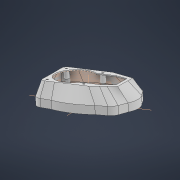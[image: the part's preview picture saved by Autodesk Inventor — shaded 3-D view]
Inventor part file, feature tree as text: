
AUTODESK INVENTOR PART (.ipt)
format: ipt  version: 2021 (Build 250183000, 183)  size: 3,913,216 bytes
history: native  units: mm
features: sketch x6, other x5, extrude x3, plane x2, surface_op x2, thicken_offset x1, loft x1
ambient origin geometry x8: Origin, YZ Plane, XZ Plane, XY Plane, X Axis, Y Axis, Z Axis, Center Point
bodies: Solid1 (feature_tree)
feature tree (20):
  sketch  "Sketch7"  dims[d14=167.0mm d15=119.0mm d16=3.8mm d18=3.8mm d19=3.8mm d20=3.8mm d22=5.0mm d23=10.0mm d24=10.0mm d25=10.0mm d26=10.0mm d27=12.0mm d28=12.0mm d29=12.0mm d30=12.0mm d31=-34.0mm d32=27.925268mm d33=118.0mm d34=82.0mm d35=10.0mm d47=10.0mm d48=10.0mm d49=100.0mm d50=25.0mm d51=25.0mm d52=8.0mm d53=8.0mm d54=0.0mm d55=90.0deg d56=0.0mm d57=90.0deg d58=10.0mm d59=0.0mm d60=2.49mm d61=20.0mm d62=20.0mm d63=0.0mm d64=20.0mm d65=0.0mm]
  plane  "Work Plane1"
  sketch  "Sketch2"  dims[d2=5.8mm d4=45.0deg]
  sketch  "Sketch1"  dims[d0=54.0mm d1=127.0mm]
  plane  "Work Plane2"
  sketch  "Sketch4"  dims[d11=83.5mm d12=59.5mm]
  sketch  "Sketch3"  dims[d6=40.0mm d8=360.0deg d10=83.5mm]
  surface_op  "Stitch Surface1"
  thicken_offset  "Thicken1"
  extrude  "Extrusion1"  Depth=127.0mm
  extrude  "Extrusion2"  TaperAngle=45.0deg  [1 undecoded]
  other  "Srf4"
  other  "Srf5"
  other  "Srf6"
  other  "Srf7"
  sketch  "Sketch6"  dims[d13=59.5mm]
  other  "Image1"
  loft  "LoftSrf2"
  extrude  "ExtrusionSrf2"  Depth=59.5mm
  surface_op  "Boundary Patch2"
note: 1 required parameter value undecoded (feature->parameter linkage not recoverable at this tier; creation-order binding heuristic only, values carry confidence <= 0.55)
